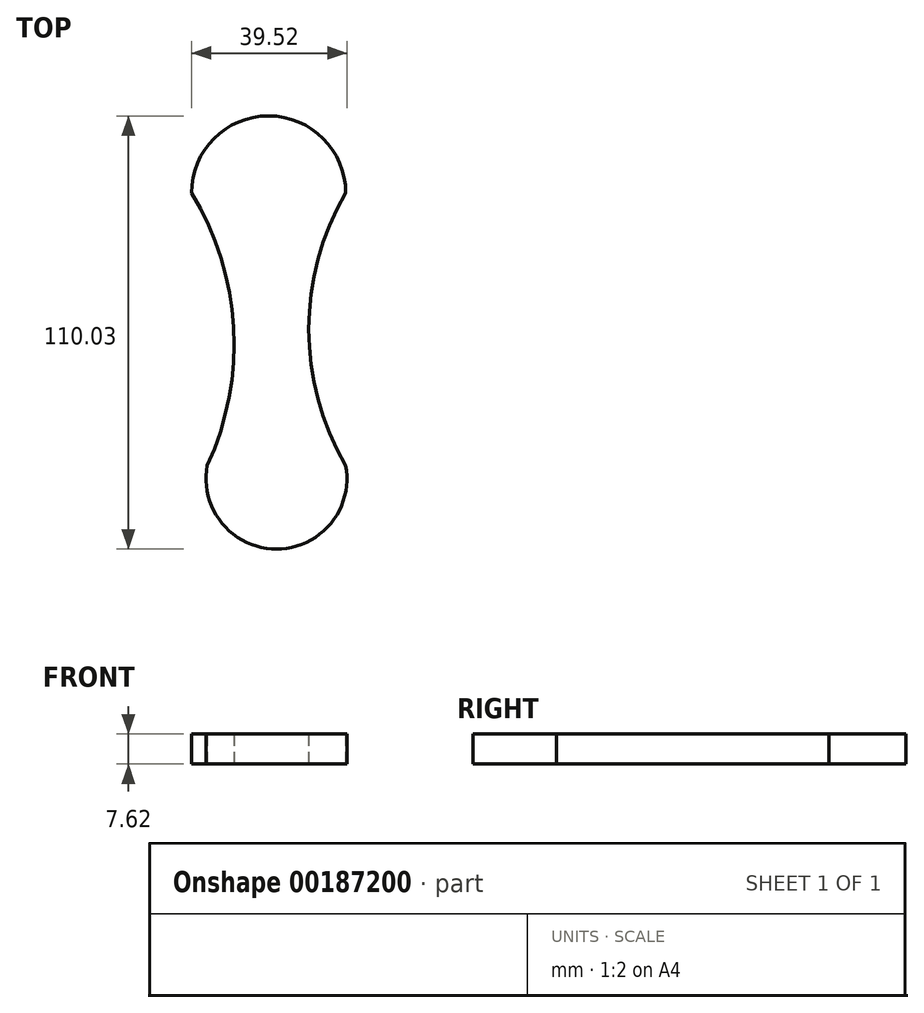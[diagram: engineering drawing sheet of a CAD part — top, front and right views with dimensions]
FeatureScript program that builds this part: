
annotation { "Feature Type Name" : "Feature", "Feature Type Description" : "" }
export const myFeature = defineFeature(function(context is Context, id is Id, definition is map)
    precondition{}
    {
        {
            var Q0;
            Q0=qCreatedBy(makeId("Top.planeOp"),FACE);
            var sketch = newSketch(context, id + "F0", { "sketchPlane" : qUnion([Q0])});
            skArc(sketch, "E0", {"start": v(-22.18, -34.2) * mm, "mid": v(-15.48, 0.88) * mm, "end": v(-26.2, 34.96) * mm});
            skArc(sketch, "E1", {"start": v(-22.18, -34.2) * mm, "mid": v(-21.9, -42.13) * mm, "end": v(-18.23, -49.15) * mm});
            skArc(sketch, "E2", {"start": v(-18.23, 50.74) * mm, "mid": v(-24.1, 43.8) * mm, "end": v(-26.2, 34.96) * mm});
            skArc(sketch, "E3", {"start": v(-18.23, -49.15) * mm, "mid": v(3.14, -53.7) * mm, "end": v(13, -34.2) * mm});
            skArc(sketch, "E4", {"start": v(13, 34.96) * mm, "mid": v(3.6, 0.38) * mm, "end": v(13, -34.2) * mm});
            skArc(sketch, "E5", {"start": v(13, 34.96) * mm, "mid": v(2.24, 52.46) * mm, "end": v(-18.23, 50.74) * mm});
            skSolve(sketch);
        }
        {
            var Q0;
            Q0=makeQuery(id+"F0.imprint","IMPRINT",FACE,{"disambiguationData":[TD([[makeQuery(id+"F0.imprint","IMPRINT",EDGE,{"derivedFrom":sQuery(id+"F0.wireOp",EDGE,"E0")}),-1.0]])]});
            extrude(context, id + "F1", {"entities" : qUnion([Q0]), "depth" : 7.62 * mm});
        }
    });
